# Revit family: Cim 746
name_source: partatom
category: Attrezzatura meccanica
revit_build: Autodesk Revit 2016 (Build: 20160126_1600(x64)
units: mm (PartAtom-declared; Revit-internal decimal feet)

## family parameters
Basato su piano di lavoro = No
Condiviso = Sì
Numero OmniClass = 23.75.00.00
Punto di calcolo locali = No
Quota connettore circolare = Usa diametro
Sempre verticale = Sì
Taglio con vuoti quando caricato = No
Tipo di parte = Normale
Titolo OmniClass = Climate Control (HVAC)

## types (6) — shared parameters
CR Brass = Brass
Descrizione = Combined manual presetting valve
Fluids = Water and Glycol
Max. flow temperature = 120°C
Max. static working pressure = 25   bar
Min. temperature = -10°C
Modello = Cim 746
Produttore = Cimberio
Technical Data Sheet = http://web.cimberio.it
URL = http://www.cimberio.it

## per-type parameters (varying)
| type | CHa | CHb | Ca | Cb | Cc | Cd | Ce | DN | DN/2 | Hch | Kv | Kvs | R1 | R2 | R3 | R4 | Sch | Technical Code | Weight | di | di1 | di2 | h | l |
| DN 15 1/2''x1/2'' | 24 mm | 24 mm | 3 mm  [stored 0.00984252 ft] | 5 mm  [stored 0.0164042 ft] | 12 mm  [stored 0.0393701 ft] | 8 mm  [stored 0.0262467 ft] | 18 mm  [stored 0.0590551 ft] | 15 mm  [stored 0.0492126 ft] | 8 mm  [stored 0.0262467 ft] | 14 mm  [stored 0.0459318 ft] | 0.47 - 2 | 2.3 | 8 mm  [stored 0.0262467 ft] | 9 mm  [stored 0.0295276 ft] | 10 mm  [stored 0.0328084 ft] | 12 mm  [stored 0.0393701 ft] | 13 mm | DA03941015 | 375   Grms. | 31 mm  [stored 0.101706 ft] | 41 mm  [stored 0.134514 ft] | 10 mm  [stored 0.0328084 ft] | 26 mm | 13 mm |
| DN 20 3/4''x3/4'' | 32 mm  [stored 0.104987 ft] | 23 mm  [stored 0.0754593 ft] | 5 mm  [stored 0.0164042 ft] | 13 mm | 4 mm  [stored 0.0131234 ft] | 7 mm  [stored 0.0229659 ft] | 24 mm | 20 mm  [stored 0.0656168 ft] | 10 mm  [stored 0.0328084 ft] | 16 mm  [stored 0.0524934 ft] | 0.54 - 3.88 | 5.3 | 10 mm  [stored 0.0328084 ft] | 12 mm  [stored 0.0393701 ft] | 11 mm  [stored 0.0360892 ft] | 13 mm | 15 mm  [stored 0.0492126 ft] | DA03941020 | 430 Grms. | 31 mm  [stored 0.101706 ft] | 41 mm  [stored 0.134514 ft] | 10 mm  [stored 0.0328084 ft] | 26 mm | 14 mm  [stored 0.0459318 ft] |
| DN 25 1"x1" | 42 mm | 25 mm  [stored 0.082021 ft] | 5 mm  [stored 0.0164042 ft] | 10 mm  [stored 0.0328084 ft] | 4 mm  [stored 0.0131234 ft] | 11 mm  [stored 0.0360892 ft] | 34 mm | 25 mm  [stored 0.082021 ft] | 13 mm | 20 mm  [stored 0.0656168 ft] | 0.96 - 7.28 | 9.2 | 12 mm  [stored 0.0393701 ft] | 16 mm  [stored 0.0524934 ft] | 15 mm  [stored 0.0492126 ft] | 17 mm | 16 mm  [stored 0.0524934 ft] | DA03941025 | 515 Grms. | 35 mm  [stored 0.114829 ft] | 45 mm  [stored 0.147638 ft] | 15 mm  [stored 0.0492126 ft] | 30 mm  [stored 0.0984252 ft] | 16 mm  [stored 0.0524934 ft] |
| DN 32 1.1/4"x1.1/4" | 50 mm  [stored 0.164042 ft] | 29 mm | 10 mm  [stored 0.0328084 ft] | 12 mm  [stored 0.0393701 ft] | 14 mm  [stored 0.0459318 ft] | 3 mm  [stored 0.00984252 ft] | 37 mm  [stored 0.121391 ft] | 32 mm  [stored 0.104987 ft] | 16 mm  [stored 0.0524934 ft] | 25 mm  [stored 0.082021 ft] | 1.56 - 13.39 | 19 | 13 mm | 18 mm  [stored 0.0590551 ft] | 18 mm  [stored 0.0590551 ft] | 20 mm  [stored 0.0656168 ft] | 20 mm  [stored 0.0656168 ft] | DA03941032 | 860 Grms. | 41 mm  [stored 0.134514 ft] | 51 mm | 15 mm  [stored 0.0492126 ft] | 36 mm  [stored 0.11811 ft] | 22 mm  [stored 0.0721785 ft] |
| DN 40 1.1/2"x1.1/2" | 63 mm | 41 mm  [stored 0.134514 ft] | 10 mm  [stored 0.0328084 ft] | 11 mm  [stored 0.0360892 ft] | 28 mm | 3 mm  [stored 0.00984252 ft] | 50 mm  [stored 0.164042 ft] | 40 mm  [stored 0.131234 ft] | 20 mm  [stored 0.0656168 ft] | 30 mm  [stored 0.0984252 ft] | 3.37 - 18.69 | 22.1 | 15 mm  [stored 0.0492126 ft] | 21 mm  [stored 0.0688976 ft] | 20 mm  [stored 0.0656168 ft] | 22 mm  [stored 0.0721785 ft] | 20 mm  [stored 0.0656168 ft] | DA03941040 | 1340 Grms. | 60 mm | 70 mm | 20 mm  [stored 0.0656168 ft] | 55 mm  [stored 0.180446 ft] | 30 mm  [stored 0.0984252 ft] |
| DN 50 2"x2" | 70 mm | 43 mm  [stored 0.141076 ft] | 11 mm  [stored 0.0360892 ft] | 14 mm  [stored 0.0459318 ft] | 26 mm | 4 mm  [stored 0.0131234 ft] | 56 mm | 50 mm  [stored 0.164042 ft] | 25 mm  [stored 0.082021 ft] | 35 mm  [stored 0.114829 ft] | 4.39 - 30.10 | 42.3 | 15 mm  [stored 0.0492126 ft] | 21 mm  [stored 0.0688976 ft] | 23 mm  [stored 0.0754593 ft] | 25 mm  [stored 0.082021 ft] | 25 mm  [stored 0.082021 ft] | DA03941050 | 1470 Grms. | 60 mm | 70 mm | 20 mm  [stored 0.0656168 ft] | 55 mm  [stored 0.180446 ft] | 30 mm  [stored 0.0984252 ft] |

note: [stored X ft] marks values corroborated as IEEE doubles in the binary element streams (Revit-internal decimal feet)

## geometry (parser evidence)
native form markers: Sweep x11
no freeform markers — native parametric forms only
